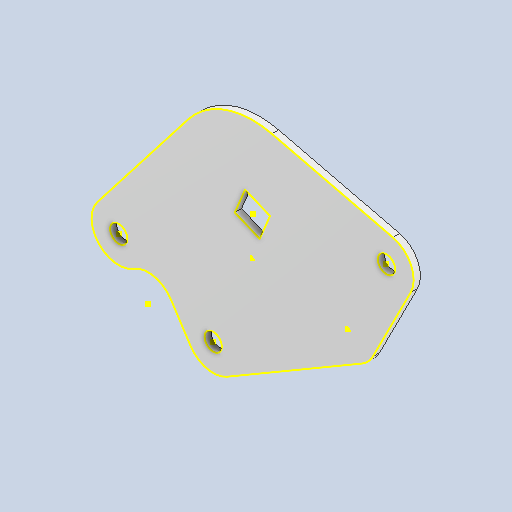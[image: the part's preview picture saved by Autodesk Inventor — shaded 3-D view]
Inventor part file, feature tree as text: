
AUTODESK INVENTOR PART (.ipt)
format: ipt  version: 2025.2 (Build 292293000, 293)  size: 246,784 bytes
history: native  units: in
note: dims shown in document units (in); Inventor stores cm internally (conversion verified against a paired STEP export)
features: other x5, sketch x2, plane x1, sheet_metal_op x1, reference x1
ambient origin geometry x8: Origin, YZ Plane, XZ Plane, XY Plane, X Axis, Y Axis, Z Axis, Center Point
bodies: Body1 (feature_tree)
feature tree (10):
  plane  "Work Plane1"
  sheet_metal_op  "Face3"
  sketch  "Sketch2"  dims[d14=0.16in d15=0.0625in]
  sketch  "Sketch1"  dims[d1=0.5in]
  reference  "Reference3"
  other  "Plate3"
  parser-record x1  (decoder bookkeeping rows leaked as tree rows — omitted from the tree; the rows remain in map.json)
  other  "ACE 2.0.iam"
  other  "V5 Rotation Sensor:4"
  other  "Rear Vertical Odom Pod Rot Side:2"
note: 1 file-system path scrubbed to <path> (originals preserved in map.json)
